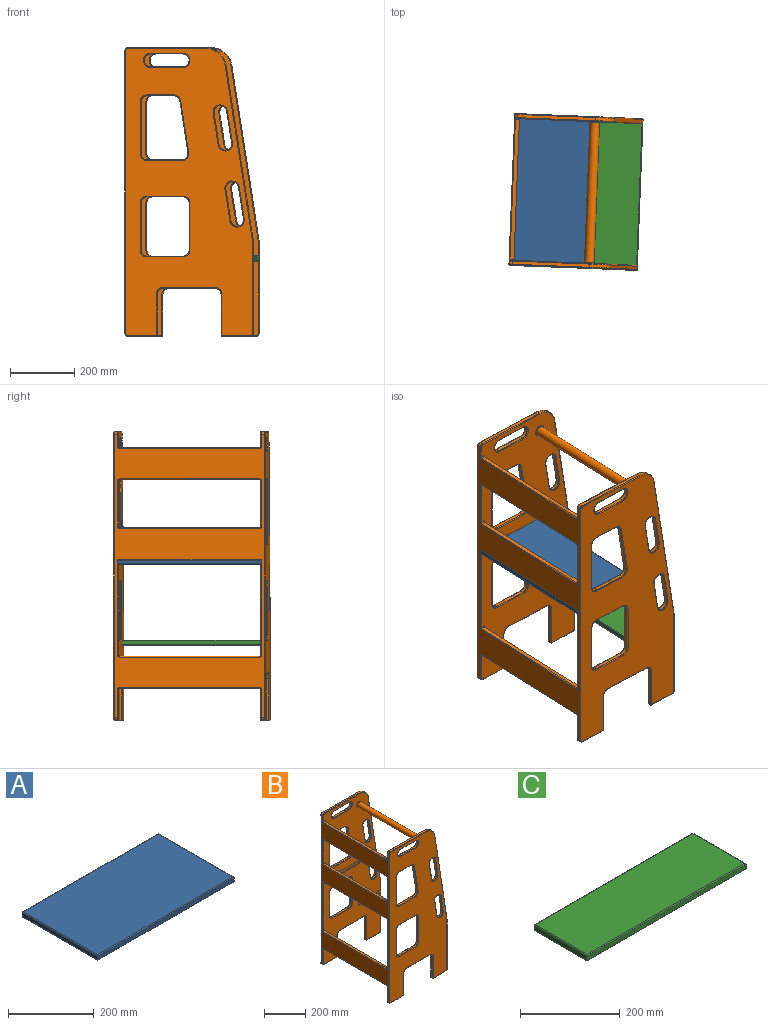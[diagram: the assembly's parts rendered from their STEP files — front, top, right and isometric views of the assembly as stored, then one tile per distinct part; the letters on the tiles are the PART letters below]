
ASSEMBLY  parts=3 mates=7
PART A: 14 faces, bbox 450x250x15 mm
  f0: plane 450x10mm, normal (0,1,0), area 4500mm2, adj f1,f3,f6,f10
  f1: plane 250x10mm, normal (-1,0,0), area 2500mm2, adj f0,f2,f7,f11
  f2: plane 450x10mm, normal (0,-1,0), area 4500mm2, adj f1,f3,f9,f13
  f3: plane 250x10mm, normal (1,0,0), area 2500mm2, adj f0,f2,f8,f12
  f4: plane 445x245mm, normal (0,0,1), area 109025mm2, adj f10,f11,f12,f13
  f5: plane 445x245mm, normal (0,0,-1), area 109025mm2, adj f6,f7,f8,f9
  f6: cylinder r=2.5mm len=450mm, axis (-1,0,0), area 1760mm2, adj f0,f5,f7,f8
  f7: cylinder r=2.5mm len=250mm, axis (0,-1,0), area 974.6mm2, adj f1,f5,f6,f9
  f8: cylinder r=2.5mm len=250mm, axis (0,1,0), area 974.6mm2, adj f3,f5,f6,f9
  f9: cylinder r=2.5mm len=450mm, axis (1,0,0), area 1760mm2, adj f2,f5,f7,f8
  f10: cylinder r=2.5mm len=450mm, axis (1,0,0), area 1760mm2, adj f0,f4,f11,f12
  f11: cylinder r=2.5mm len=250mm, axis (0,1,0), area 974.6mm2, adj f1,f4,f10,f13
  f12: cylinder r=2.5mm len=250mm, axis (0,-1,0), area 974.6mm2, adj f3,f4,f10,f13
  f13: cylinder r=2.5mm len=450mm, axis (-1,0,0), area 1760mm2, adj f2,f4,f11,f12
PART B: 341 faces, bbox 401.6x472x906.2 mm
  f0: plane 90x10mm, normal (0,0,-1), area 900mm2, adj f7,f58,f76,f109
  f1: plane 895x395mm, normal (0,-1,0), area 219137.1mm2, adj f107,f108,f109,f110,f111,f112,f113,f114
  f2: plane 895x395mm, normal (0,1,0), area 205524.9mm2, adj f62,f63,f64,f65,f66,f67,f68,f69
  f3: plane 290x10mm, normal (1,0,0), area 2892.5mm2, adj f9,f10,f22,f23,f25,f63,f71,f118
  f4: plane 240.92x10mm, normal (0,0,1), area 2409.2mm2, adj f5,f11,f77,f112
  f5: cylinder r=10mm len=10mm, axis (0,1,0), area 157.1mm2, adj f4,f6,f79,f110
  f6: plane 880x467mm, normal (-1,0,0), area 146151.2mm2, adj f5,f7,f17,f27,f28,f80,f81,f82
  f7: cylinder r=10mm len=10mm, axis (0,1,0), area 157.1mm2, adj f0,f6,f78,f107
  f8: plane 90x10mm, normal (0,0,-1), area 900mm2, adj f9,f59,f64,f121
  f9: cylinder r=10mm len=10mm, axis (0,1,0), area 157.1mm2, adj f3,f8,f62,f120
  f10: plane 545x84.86mm, normal (0.99,0,0.15), area 5515.7mm2, adj f3,f11,f73,f116
  f11: cylinder r=65mm len=64.23mm, axis (0,1,0), area 920.6mm2, adj f4,f10,f75,f114
  f12: plane 437x100mm, normal (1,0,0), area 43700mm2, adj f13,f14,f89,f255
  f13: plane 437x12.5mm, normal (0,0,1), area 5462.5mm2, adj f12,f83,f87,f253
  f14: plane 437x12.5mm, normal (0,0,-1), area 5462.5mm2, adj f12,f92,f93,f257
  f15: plane 437x97.5mm, normal (1,0,0), area 42607.5mm2, adj f16,f104,f106,f267
  f16: plane 437x12.5mm, normal (0,0,1), area 5462.5mm2, adj f15,f98,f102,f265
  f17: plane 448x250mm, normal (0,0,-1), area 5848.2mm2, adj f6,f26,f28,f103,f105,f106,f194,f196
  f18: plane 437x100mm, normal (1,0,0), area 43700mm2, adj f19,f20,f88,f254
  f19: plane 437x12.5mm, normal (0,0,1), area 5462.5mm2, adj f18,f90,f91,f256
  f20: plane 437x12.5mm, normal (0,0,-1), area 5462.5mm2, adj f18,f80,f86,f252
  f21: cylinder r=15mm len=437mm, axis (0,-1,0), area 41186.3mm2, adj f178,f340
  f22: plane 150x0.5mm, normal (0,0,-1), area 75mm2, adj f3,f24,f25,f69
  f23: plane 150x0.5mm, normal (0,0,1), area 75mm2, adj f3,f24,f25,f65
  f24: plane 15x0.5mm, normal (1,0,0), area 7.5mm2, adj f22,f23,f25,f67
  f25: plane 150x15mm, normal (0,1,0), area 2250mm2, adj f3,f22,f23,f24
  f26: plane 15x0.5mm, normal (-1,0,0), area 7.5mm2, adj f17,f27,f28,f101
  f27: plane 250x0.5mm, normal (0,0,1), area 125mm2, adj f6,f26,f28,f99
  f28: plane 250x15mm, normal (0,1,0), area 3750mm2, adj f6,f17,f26,f27
  f29: cylinder r=20mm len=39.76mm, axis (0,1,0), area 628.3mm2, adj f30,f32,f171,f175
  f30: plane 98.81x15.38mm, normal (0.99,0,0.15), area 1000mm2, adj f29,f31,f173,f177
  f31: cylinder r=20mm len=39.76mm, axis (0,1,0), area 628.3mm2, adj f30,f32,f172,f176
  f32: plane 98.81x15.38mm, normal (-0.99,0,-0.15), area 1000mm2, adj f29,f31,f170,f174
  f33: plane 110x10mm, normal (0,0,-1), area 1100mm2, adj f34,f40,f127,f135
  f34: cylinder r=20mm len=20mm, axis (0,1,0), area 314.2mm2, adj f33,f35,f129,f137
  f35: plane 145x10mm, normal (1,0,0), area 1450mm2, adj f34,f36,f128,f136
  f36: cylinder r=20mm len=20mm, axis (0,1,0), area 314.2mm2, adj f35,f37,f126,f134
  f37: plane 110x10mm, normal (0,0,1), area 1100mm2, adj f36,f38,f124,f132
  f38: cylinder r=20mm len=20mm, axis (0,1,0), area 314.2mm2, adj f37,f39,f122,f130
  f39: plane 145x10mm, normal (-1,0,0), area 1450mm2, adj f38,f40,f123,f131
  f40: cylinder r=20mm len=20mm, axis (0,1,0), area 314.2mm2, adj f33,f39,f125,f133
  f41: plane 81.73x10mm, normal (0,0,-1), area 817.3mm2, adj f42,f48,f143,f151
  f42: cylinder r=20mm len=20mm, axis (0,1,0), area 314.2mm2, adj f41,f43,f145,f153
  f43: plane 160x10mm, normal (1,0,0), area 1600mm2, adj f42,f44,f144,f152
  f44: cylinder r=20mm len=20mm, axis (0,1,0), area 314.2mm2, adj f43,f45,f142,f150
  f45: plane 106.65x10mm, normal (0,0,1), area 1066.5mm2, adj f44,f46,f140,f148
  f46: cylinder r=20mm len=23.08mm, axis (0,1,0), area 345.1mm2, adj f45,f47,f138,f146
  f47: plane 160x24.91mm, normal (-0.99,0,-0.15), area 1619.3mm2, adj f46,f48,f139,f147
  f48: cylinder r=20mm len=19.76mm, axis (0,1,0), area 283.3mm2, adj f41,f47,f141,f149
  f49: cylinder r=20mm len=40mm, axis (0,1,0), area 628.3mm2, adj f50,f52,f155,f159
  f50: plane 100x10mm, normal (0,0,1), area 1000mm2, adj f49,f51,f157,f161
  f51: cylinder r=20mm len=40mm, axis (0,1,0), area 628.3mm2, adj f50,f52,f156,f160
  f52: plane 100x10mm, normal (0,0,-1), area 1000mm2, adj f49,f51,f154,f158
  f53: cylinder r=20mm len=39.76mm, axis (0,1,0), area 628.3mm2, adj f54,f56,f162,f166
  f54: plane 98.81x15.38mm, normal (0.99,0,0.15), area 1000mm2, adj f53,f55,f163,f167
  f55: cylinder r=20mm len=39.76mm, axis (0,1,0), area 628.3mm2, adj f54,f56,f165,f169
  f56: plane 98.81x15.38mm, normal (-0.99,0,-0.15), area 1000mm2, adj f53,f55,f164,f168
  f57: cylinder r=20mm len=20mm, axis (0,1,0), area 314.2mm2, adj f58,f61,f72,f113
  f58: plane 130x10mm, normal (1,0,0), area 1300mm2, adj f0,f57,f74,f111
  f59: plane 130x10mm, normal (-1,0,0), area 1300mm2, adj f8,f60,f66,f119
  f60: cylinder r=20mm len=20mm, axis (0,1,0), area 314.2mm2, adj f59,f61,f68,f117
  f61: plane 160x10mm, normal (0,0,-1), area 1600mm2, adj f57,f60,f70,f115
  f62: torus R=7.5mm, axis (0,-1,0), area 56.1mm2, adj f2,f9,f63,f64
  f63: cylinder r=2.5mm len=225mm, axis (0,0,1), area 880mm2, adj f2,f3,f62,f65
  f64: cylinder r=2.5mm len=90mm, axis (1,0,0), area 349.9mm2, adj f2,f8,f62,f66
  f65: cylinder r=2.5mm len=152.5mm, axis (-1,0,0), area 589mm2, adj f2,f23,f63,f67
  f66: cylinder r=2.5mm len=130mm, axis (0,0,-1), area 506.9mm2, adj f2,f59,f64,f68
  f67: cylinder r=2.5mm len=20mm, axis (0,0,1), area 66mm2, adj f2,f24,f65,f69
  f68: torus R=22.5mm, axis (0,-1,0), area 129mm2, adj f2,f60,f66,f70
  f69: cylinder r=2.5mm len=152.5mm, axis (1,0,0), area 589mm2, adj f2,f22,f67,f71
  f70: cylinder r=2.5mm len=160mm, axis (1,0,0), area 628.3mm2, adj f2,f61,f68,f72
  f71: cylinder r=2.5mm len=50mm, axis (0,0,1), area 192.5mm2, adj f2,f3,f69,f73
  f72: torus R=22.5mm, axis (0,-1,0), area 129mm2, adj f2,f57,f70,f74
  f73: cylinder r=2.5mm len=545.38mm, axis (-0.15,0,0.99), area 2165.7mm2, adj f2,f10,f71,f75
  f74: cylinder r=2.5mm len=130mm, axis (0,0,1), area 506.9mm2, adj f2,f58,f72,f76
  f75: torus R=62.5mm, axis (0,-1,0), area 356.5mm2, adj f2,f11,f73,f77
  f76: cylinder r=2.5mm len=90mm, axis (1,0,0), area 349.9mm2, adj f0,f2,f74,f78
  f77: cylinder r=2.5mm len=240.92mm, axis (-1,0,0), area 946.1mm2, adj f2,f4,f75,f79
  f78: torus R=7.5mm, axis (0,-1,0), area 56.1mm2, adj f2,f7,f76,f81
  f79: torus R=7.5mm, axis (0,-1,0), area 56.1mm2, adj f2,f5,f77,f82
  f80: cylinder r=2.5mm len=437mm, axis (0,-1,0), area 1716.1mm2, adj f6,f20,f84,f250
  f81: cylinder r=2.5mm len=87.5mm, axis (0,0,-1), area 343.6mm2, adj f2,f6,f78,f84
  f82: cylinder r=2.5mm len=37.5mm, axis (0,0,-1), area 147.3mm2, adj f2,f6,f79,f85
  f83: cylinder r=2.5mm len=437mm, axis (0,1,0), area 1716.1mm2, adj f6,f13,f85,f251
  f84: torus R=5mm, axis (1,0,0), area 21mm2, adj f6,f80,f81,f86
  f85: torus R=5mm, axis (1,0,0), area 21mm2, adj f6,f82,f83,f87
  f86: cylinder r=2.5mm len=15mm, axis (1,0,0), area 52.7mm2, adj f2,f20,f84,f88
  f87: cylinder r=2.5mm len=15mm, axis (-1,0,0), area 52.7mm2, adj f2,f13,f85,f89
  f88: cylinder r=2.5mm len=105mm, axis (0,0,1), area 399.8mm2, adj f2,f18,f86,f91
  f89: cylinder r=2.5mm len=105mm, axis (0,0,1), area 399.8mm2, adj f2,f12,f87,f92
  f90: cylinder r=2.5mm len=437mm, axis (0,1,0), area 1716.1mm2, adj f6,f19,f94,f258
  f91: cylinder r=2.5mm len=15mm, axis (-1,0,0), area 52.7mm2, adj f2,f19,f88,f94
  f92: cylinder r=2.5mm len=15mm, axis (1,0,0), area 52.7mm2, adj f2,f14,f89,f95
  f93: cylinder r=2.5mm len=437mm, axis (0,-1,0), area 1716.1mm2, adj f6,f14,f95,f259
  f94: torus R=5mm, axis (1,0,0), area 21mm2, adj f6,f90,f91,f96
  f95: torus R=5mm, axis (1,0,0), area 21mm2, adj f6,f92,f93,f97
  f96: cylinder r=2.5mm len=282.5mm, axis (0,0,-1), area 1105.8mm2, adj f2,f6,f94,f99
  f97: cylinder r=2.5mm len=145mm, axis (0,0,-1), area 569.4mm2, adj f2,f6,f95,f100
  f98: cylinder r=2.5mm len=437mm, axis (0,1,0), area 1716.1mm2, adj f6,f16,f100,f263
  f99: cylinder r=2.5mm len=252.5mm, axis (-1,0,0), area 981.7mm2, adj f2,f27,f96,f101
  f100: torus R=5mm, axis (1,0,0), area 21mm2, adj f6,f97,f98,f102
  f101: cylinder r=2.5mm len=20mm, axis (0,0,-1), area 66mm2, adj f2,f26,f99,f103
  f102: cylinder r=2.5mm len=15mm, axis (-1,0,0), area 52.7mm2, adj f2,f16,f100,f104
  f103: cylinder r=2.5mm len=235mm, axis (-1,0,0), area 916.6mm2, adj f2,f17,f101,f105
  f104: cylinder r=2.5mm len=100mm, axis (0,0,1), area 386.4mm2, adj f2,f15,f102,f105
  f105: torus R=5mm, axis (0,0,1), area 21mm2, adj f17,f103,f104,f106
  f106: cylinder r=2.5mm len=437mm, axis (0,-1,0), area 1716.1mm2, adj f15,f17,f105,f268
  f107: torus R=7.5mm, axis (0,-1,0), area 56.1mm2, adj f1,f7,f108,f109
  f108: cylinder r=2.5mm len=880mm, axis (0,0,1), area 3455.8mm2, adj f1,f6,f107,f110
  f109: cylinder r=2.5mm len=90mm, axis (-1,0,0), area 349.9mm2, adj f0,f1,f107,f111
  f110: torus R=7.5mm, axis (0,-1,0), area 56.1mm2, adj f1,f5,f108,f112
  f111: cylinder r=2.5mm len=130mm, axis (0,0,-1), area 506.9mm2, adj f1,f58,f109,f113
  f112: cylinder r=2.5mm len=240.92mm, axis (1,0,0), area 946.1mm2, adj f1,f4,f110,f114
  f113: torus R=22.5mm, axis (0,-1,0), area 129mm2, adj f1,f57,f111,f115
  f114: torus R=62.5mm, axis (0,-1,0), area 356.5mm2, adj f1,f11,f112,f116
  f115: cylinder r=2.5mm len=160mm, axis (-1,0,0), area 628.3mm2, adj f1,f61,f113,f117
  f116: cylinder r=2.5mm len=545.38mm, axis (0.15,0,-0.99), area 2165.7mm2, adj f1,f10,f114,f118
  f117: torus R=22.5mm, axis (0,-1,0), area 129mm2, adj f1,f60,f115,f119
  f118: cylinder r=2.5mm len=290mm, axis (0,0,-1), area 1138.6mm2, adj f1,f3,f116,f120
  f119: cylinder r=2.5mm len=130mm, axis (0,0,1), area 506.9mm2, adj f1,f59,f117,f121
  f120: torus R=7.5mm, axis (0,-1,0), area 56.1mm2, adj f1,f9,f118,f121
  f121: cylinder r=2.5mm len=90mm, axis (-1,0,0), area 349.9mm2, adj f1,f8,f119,f120
  f122: torus R=22.5mm, axis (0,-1,0), area 129mm2, adj f2,f38,f123,f124
  f123: cylinder r=2.5mm len=145mm, axis (0,0,-1), area 569.4mm2, adj f2,f39,f122,f125
  f124: cylinder r=2.5mm len=110mm, axis (-1,0,0), area 432mm2, adj f2,f37,f122,f126
  f125: torus R=22.5mm, axis (0,-1,0), area 129mm2, adj f2,f40,f123,f127
  f126: torus R=22.5mm, axis (0,-1,0), area 129mm2, adj f2,f36,f124,f128
  f127: cylinder r=2.5mm len=110mm, axis (1,0,0), area 432mm2, adj f2,f33,f125,f129
  f128: cylinder r=2.5mm len=145mm, axis (0,0,1), area 569.4mm2, adj f2,f35,f126,f129
  f129: torus R=22.5mm, axis (0,-1,0), area 129mm2, adj f2,f34,f127,f128
  f130: torus R=22.5mm, axis (0,-1,0), area 129mm2, adj f1,f38,f131,f132
  f131: cylinder r=2.5mm len=145mm, axis (0,0,1), area 569.4mm2, adj f1,f39,f130,f133
  f132: cylinder r=2.5mm len=110mm, axis (1,0,0), area 432mm2, adj f1,f37,f130,f134
  f133: torus R=22.5mm, axis (0,-1,0), area 129mm2, adj f1,f40,f131,f135
  f134: torus R=22.5mm, axis (0,-1,0), area 129mm2, adj f1,f36,f132,f136
  f135: cylinder r=2.5mm len=110mm, axis (-1,0,0), area 432mm2, adj f1,f33,f133,f137
  f136: cylinder r=2.5mm len=145mm, axis (0,0,-1), area 569.4mm2, adj f1,f35,f134,f137
  f137: torus R=22.5mm, axis (0,-1,0), area 129mm2, adj f1,f34,f135,f136
  f138: torus R=22.5mm, axis (0,-1,0), area 141.7mm2, adj f2,f46,f139,f140
  f139: cylinder r=2.5mm len=160.38mm, axis (0.15,0,-0.99), area 635.9mm2, adj f2,f47,f138,f141
  f140: cylinder r=2.5mm len=106.65mm, axis (-1,0,0), area 418.8mm2, adj f2,f45,f138,f142
  f141: torus R=22.5mm, axis (0,-1,0), area 116.3mm2, adj f2,f48,f139,f143
  f142: torus R=22.5mm, axis (0,-1,0), area 129mm2, adj f2,f44,f140,f144
  f143: cylinder r=2.5mm len=81.73mm, axis (1,0,0), area 321mm2, adj f2,f41,f141,f145
  f144: cylinder r=2.5mm len=160mm, axis (0,0,1), area 628.3mm2, adj f2,f43,f142,f145
  f145: torus R=22.5mm, axis (0,-1,0), area 129mm2, adj f2,f42,f143,f144
  f146: torus R=22.5mm, axis (0,-1,0), area 141.7mm2, adj f1,f46,f147,f148
  f147: cylinder r=2.5mm len=160.38mm, axis (-0.15,0,0.99), area 635.9mm2, adj f1,f47,f146,f149
  f148: cylinder r=2.5mm len=106.65mm, axis (1,0,0), area 418.8mm2, adj f1,f45,f146,f150
  f149: torus R=22.5mm, axis (0,-1,0), area 116.3mm2, adj f1,f48,f147,f151
  f150: torus R=22.5mm, axis (0,-1,0), area 129mm2, adj f1,f44,f148,f152
  f151: cylinder r=2.5mm len=81.73mm, axis (-1,0,0), area 321mm2, adj f1,f41,f149,f153
  f152: cylinder r=2.5mm len=160mm, axis (0,0,-1), area 628.3mm2, adj f1,f43,f150,f153
  f153: torus R=22.5mm, axis (0,-1,0), area 129mm2, adj f1,f42,f151,f152
  f154: cylinder r=2.5mm len=100mm, axis (1,0,0), area 392.7mm2, adj f2,f52,f155,f156
  f155: torus R=22.5mm, axis (0,-1,0), area 257.9mm2, adj f2,f49,f154,f157
  f156: torus R=22.5mm, axis (0,-1,0), area 257.9mm2, adj f2,f51,f154,f157
  f157: cylinder r=2.5mm len=100mm, axis (-1,0,0), area 392.7mm2, adj f2,f50,f155,f156
  f158: cylinder r=2.5mm len=100mm, axis (-1,0,0), area 392.7mm2, adj f1,f52,f159,f160
  f159: torus R=22.5mm, axis (0,-1,0), area 257.9mm2, adj f1,f49,f158,f161
  f160: torus R=22.5mm, axis (0,-1,0), area 257.9mm2, adj f1,f51,f158,f161
  f161: cylinder r=2.5mm len=100mm, axis (1,0,0), area 392.7mm2, adj f1,f50,f159,f160
  f162: torus R=22.5mm, axis (0,-1,0), area 257.9mm2, adj f2,f53,f163,f164
  f163: cylinder r=2.5mm len=99.19mm, axis (-0.15,0,0.99), area 392.7mm2, adj f2,f54,f162,f165
  f164: cylinder r=2.5mm len=99.19mm, axis (0.15,0,-0.99), area 392.7mm2, adj f2,f56,f162,f165
  f165: torus R=22.5mm, axis (0,-1,0), area 257.9mm2, adj f2,f55,f163,f164
  f166: torus R=22.5mm, axis (0,-1,0), area 257.9mm2, adj f1,f53,f167,f168
  f167: cylinder r=2.5mm len=99.19mm, axis (0.15,0,-0.99), area 392.7mm2, adj f1,f54,f166,f169
  f168: cylinder r=2.5mm len=99.19mm, axis (-0.15,0,0.99), area 392.7mm2, adj f1,f56,f166,f169
  f169: torus R=22.5mm, axis (0,-1,0), area 257.9mm2, adj f1,f55,f167,f168
  f170: cylinder r=2.5mm len=99.19mm, axis (0.15,0,-0.99), area 392.7mm2, adj f2,f32,f171,f172
  f171: torus R=22.5mm, axis (0,-1,0), area 257.9mm2, adj f2,f29,f170,f173
  f172: torus R=22.5mm, axis (0,-1,0), area 257.9mm2, adj f2,f31,f170,f173
  f173: cylinder r=2.5mm len=99.19mm, axis (-0.15,0,0.99), area 392.7mm2, adj f2,f30,f171,f172
  f174: cylinder r=2.5mm len=99.19mm, axis (-0.15,0,0.99), area 392.7mm2, adj f1,f32,f175,f176
  f175: torus R=22.5mm, axis (0,-1,0), area 257.9mm2, adj f1,f29,f174,f177
  f176: torus R=22.5mm, axis (0,-1,0), area 257.9mm2, adj f1,f31,f174,f177
  f177: cylinder r=2.5mm len=99.19mm, axis (0.15,0,-0.99), area 392.7mm2, adj f1,f30,f175,f176
  f178: torus R=17.5mm, axis (0,-1,0), area 392.5mm2, adj f2,f21
  f179: plane 90x10mm, normal (0,0,-1), area 900mm2, adj f185,f226,f244,f271
  f180: plane 895x395mm, normal (0,1,0), area 219137.1mm2, adj f269,f270,f271,f272,f273,f274,f275,f276
  f181: plane 895x395mm, normal (0,-1,0), area 205524.9mm2, adj f230,f231,f232,f233,f234,f235,f236,f237
  f182: plane 290x10mm, normal (1,0,0), area 2892.5mm2, adj f187,f188,f190,f191,f193,f231,f239,f280
  f183: plane 240.92x10mm, normal (0,0,1), area 2409.2mm2, adj f184,f189,f245,f274
  f184: cylinder r=10mm len=10mm, axis (0,-1,0), area 157.1mm2, adj f6,f183,f247,f272
  f185: cylinder r=10mm len=10mm, axis (0,-1,0), area 157.1mm2, adj f6,f179,f246,f269
  f186: plane 90x10mm, normal (0,0,-1), area 900mm2, adj f187,f227,f232,f283
  f187: cylinder r=10mm len=10mm, axis (0,-1,0), area 157.1mm2, adj f182,f186,f230,f282
  f188: plane 545x84.86mm, normal (0.99,0,0.15), area 5515.7mm2, adj f182,f189,f241,f278
  f189: cylinder r=65mm len=64.23mm, axis (0,-1,0), area 920.6mm2, adj f183,f188,f243,f276
  f190: plane 150x0.5mm, normal (0,0,-1), area 75mm2, adj f182,f192,f193,f237
  f191: plane 150x0.5mm, normal (0,0,1), area 75mm2, adj f182,f192,f193,f233
  f192: plane 15x0.5mm, normal (1,0,0), area 7.5mm2, adj f190,f191,f193,f235
  f193: plane 150x15mm, normal (0,-1,0), area 2250mm2, adj f182,f190,f191,f192
  f194: plane 15x0.5mm, normal (-1,0,0), area 7.5mm2, adj f17,f195,f196,f264
  f195: plane 250x0.5mm, normal (0,0,1), area 125mm2, adj f6,f194,f196,f262
  f196: plane 250x15mm, normal (0,-1,0), area 3750mm2, adj f6,f17,f194,f195
  f197: cylinder r=20mm len=39.76mm, axis (0,-1,0), area 628.3mm2, adj f198,f200,f333,f337
  f198: plane 98.81x15.38mm, normal (0.99,0,0.15), area 1000mm2, adj f197,f199,f335,f339
  f199: cylinder r=20mm len=39.76mm, axis (0,-1,0), area 628.3mm2, adj f198,f200,f334,f338
  f200: plane 98.81x15.38mm, normal (-0.99,0,-0.15), area 1000mm2, adj f197,f199,f332,f336
  f201: plane 110x10mm, normal (0,0,-1), area 1100mm2, adj f202,f208,f289,f297
  f202: cylinder r=20mm len=20mm, axis (0,-1,0), area 314.2mm2, adj f201,f203,f291,f299
  f203: plane 145x10mm, normal (1,0,0), area 1450mm2, adj f202,f204,f290,f298
  f204: cylinder r=20mm len=20mm, axis (0,-1,0), area 314.2mm2, adj f203,f205,f288,f296
  f205: plane 110x10mm, normal (0,0,1), area 1100mm2, adj f204,f206,f286,f294
  f206: cylinder r=20mm len=20mm, axis (0,-1,0), area 314.2mm2, adj f205,f207,f284,f292
  f207: plane 145x10mm, normal (-1,0,0), area 1450mm2, adj f206,f208,f285,f293
  f208: cylinder r=20mm len=20mm, axis (0,-1,0), area 314.2mm2, adj f201,f207,f287,f295
  f209: plane 81.73x10mm, normal (0,0,-1), area 817.3mm2, adj f210,f216,f305,f313
  f210: cylinder r=20mm len=20mm, axis (0,-1,0), area 314.2mm2, adj f209,f211,f307,f315
  f211: plane 160x10mm, normal (1,0,0), area 1600mm2, adj f210,f212,f306,f314
  f212: cylinder r=20mm len=20mm, axis (0,-1,0), area 314.2mm2, adj f211,f213,f304,f312
  f213: plane 106.65x10mm, normal (0,0,1), area 1066.5mm2, adj f212,f214,f302,f310
  f214: cylinder r=20mm len=23.08mm, axis (0,-1,0), area 345.1mm2, adj f213,f215,f300,f308
  f215: plane 160x24.91mm, normal (-0.99,0,-0.15), area 1619.3mm2, adj f214,f216,f301,f309
  f216: cylinder r=20mm len=19.76mm, axis (0,-1,0), area 283.3mm2, adj f209,f215,f303,f311
  f217: cylinder r=20mm len=40mm, axis (0,-1,0), area 628.3mm2, adj f218,f220,f317,f321
  f218: plane 100x10mm, normal (0,0,1), area 1000mm2, adj f217,f219,f319,f323
  f219: cylinder r=20mm len=40mm, axis (0,-1,0), area 628.3mm2, adj f218,f220,f318,f322
  f220: plane 100x10mm, normal (0,0,-1), area 1000mm2, adj f217,f219,f316,f320
  f221: cylinder r=20mm len=39.76mm, axis (0,-1,0), area 628.3mm2, adj f222,f224,f324,f328
  f222: plane 98.81x15.38mm, normal (0.99,0,0.15), area 1000mm2, adj f221,f223,f325,f329
  f223: cylinder r=20mm len=39.76mm, axis (0,-1,0), area 628.3mm2, adj f222,f224,f327,f331
  f224: plane 98.81x15.38mm, normal (-0.99,0,-0.15), area 1000mm2, adj f221,f223,f326,f330
  f225: cylinder r=20mm len=20mm, axis (0,-1,0), area 314.2mm2, adj f226,f229,f240,f275
  f226: plane 130x10mm, normal (1,0,0), area 1300mm2, adj f179,f225,f242,f273
  f227: plane 130x10mm, normal (-1,0,0), area 1300mm2, adj f186,f228,f234,f281
  f228: cylinder r=20mm len=20mm, axis (0,-1,0), area 314.2mm2, adj f227,f229,f236,f279
  f229: plane 160x10mm, normal (0,0,-1), area 1600mm2, adj f225,f228,f238,f277
  f230: torus R=7.5mm, axis (0,1,0), area 56.1mm2, adj f181,f187,f231,f232
  f231: cylinder r=2.5mm len=225mm, axis (0,0,1), area 880mm2, adj f181,f182,f230,f233
  f232: cylinder r=2.5mm len=90mm, axis (1,0,0), area 349.9mm2, adj f181,f186,f230,f234
  f233: cylinder r=2.5mm len=152.5mm, axis (-1,0,0), area 589mm2, adj f181,f191,f231,f235
  f234: cylinder r=2.5mm len=130mm, axis (0,0,-1), area 506.9mm2, adj f181,f227,f232,f236
  f235: cylinder r=2.5mm len=20mm, axis (0,0,1), area 66mm2, adj f181,f192,f233,f237
  f236: torus R=22.5mm, axis (0,1,0), area 129mm2, adj f181,f228,f234,f238
  f237: cylinder r=2.5mm len=152.5mm, axis (1,0,0), area 589mm2, adj f181,f190,f235,f239
  f238: cylinder r=2.5mm len=160mm, axis (1,0,0), area 628.3mm2, adj f181,f229,f236,f240
  f239: cylinder r=2.5mm len=50mm, axis (0,0,1), area 192.5mm2, adj f181,f182,f237,f241
  f240: torus R=22.5mm, axis (0,1,0), area 129mm2, adj f181,f225,f238,f242
  f241: cylinder r=2.5mm len=545.38mm, axis (-0.15,0,0.99), area 2165.7mm2, adj f181,f188,f239,f243
  f242: cylinder r=2.5mm len=130mm, axis (0,0,1), area 506.9mm2, adj f181,f226,f240,f244
  f243: torus R=62.5mm, axis (0,1,0), area 356.5mm2, adj f181,f189,f241,f245
  f244: cylinder r=2.5mm len=90mm, axis (1,0,0), area 349.9mm2, adj f179,f181,f242,f246
  f245: cylinder r=2.5mm len=240.92mm, axis (-1,0,0), area 946.1mm2, adj f181,f183,f243,f247
  f246: torus R=7.5mm, axis (0,1,0), area 56.1mm2, adj f181,f185,f244,f248
  f247: torus R=7.5mm, axis (0,1,0), area 56.1mm2, adj f181,f184,f245,f249
  f248: cylinder r=2.5mm len=87.5mm, axis (0,0,-1), area 343.6mm2, adj f6,f181,f246,f250
  f249: cylinder r=2.5mm len=37.5mm, axis (0,0,-1), area 147.3mm2, adj f6,f181,f247,f251
  f250: torus R=5mm, axis (1,0,0), area 21mm2, adj f6,f80,f248,f252
  f251: torus R=5mm, axis (1,0,0), area 21mm2, adj f6,f83,f249,f253
  f252: cylinder r=2.5mm len=15mm, axis (1,0,0), area 52.7mm2, adj f20,f181,f250,f254
  f253: cylinder r=2.5mm len=15mm, axis (-1,0,0), area 52.7mm2, adj f13,f181,f251,f255
  f254: cylinder r=2.5mm len=105mm, axis (0,0,1), area 399.8mm2, adj f18,f181,f252,f256
  f255: cylinder r=2.5mm len=105mm, axis (0,0,1), area 399.8mm2, adj f12,f181,f253,f257
  f256: cylinder r=2.5mm len=15mm, axis (-1,0,0), area 52.7mm2, adj f19,f181,f254,f258
  f257: cylinder r=2.5mm len=15mm, axis (1,0,0), area 52.7mm2, adj f14,f181,f255,f259
  f258: torus R=5mm, axis (1,0,0), area 21mm2, adj f6,f90,f256,f260
  f259: torus R=5mm, axis (1,0,0), area 21mm2, adj f6,f93,f257,f261
  f260: cylinder r=2.5mm len=282.5mm, axis (0,0,-1), area 1105.8mm2, adj f6,f181,f258,f262
  f261: cylinder r=2.5mm len=145mm, axis (0,0,-1), area 569.4mm2, adj f6,f181,f259,f263
  f262: cylinder r=2.5mm len=252.5mm, axis (-1,0,0), area 981.7mm2, adj f181,f195,f260,f264
  f263: torus R=5mm, axis (1,0,0), area 21mm2, adj f6,f98,f261,f265
  f264: cylinder r=2.5mm len=20mm, axis (0,0,-1), area 66mm2, adj f181,f194,f262,f266
  f265: cylinder r=2.5mm len=15mm, axis (-1,0,0), area 52.7mm2, adj f16,f181,f263,f267
  f266: cylinder r=2.5mm len=235mm, axis (-1,0,0), area 916.6mm2, adj f17,f181,f264,f268
  f267: cylinder r=2.5mm len=100mm, axis (0,0,1), area 386.4mm2, adj f15,f181,f265,f268
  f268: torus R=5mm, axis (0,0,1), area 21mm2, adj f17,f106,f266,f267
  f269: torus R=7.5mm, axis (0,1,0), area 56.1mm2, adj f180,f185,f270,f271
  f270: cylinder r=2.5mm len=880mm, axis (0,0,1), area 3455.8mm2, adj f6,f180,f269,f272
  f271: cylinder r=2.5mm len=90mm, axis (-1,0,0), area 349.9mm2, adj f179,f180,f269,f273
  f272: torus R=7.5mm, axis (0,1,0), area 56.1mm2, adj f180,f184,f270,f274
  f273: cylinder r=2.5mm len=130mm, axis (0,0,-1), area 506.9mm2, adj f180,f226,f271,f275
  f274: cylinder r=2.5mm len=240.92mm, axis (1,0,0), area 946.1mm2, adj f180,f183,f272,f276
  f275: torus R=22.5mm, axis (0,1,0), area 129mm2, adj f180,f225,f273,f277
  f276: torus R=62.5mm, axis (0,1,0), area 356.5mm2, adj f180,f189,f274,f278
  f277: cylinder r=2.5mm len=160mm, axis (-1,0,0), area 628.3mm2, adj f180,f229,f275,f279
  f278: cylinder r=2.5mm len=545.38mm, axis (0.15,0,-0.99), area 2165.7mm2, adj f180,f188,f276,f280
  f279: torus R=22.5mm, axis (0,1,0), area 129mm2, adj f180,f228,f277,f281
  f280: cylinder r=2.5mm len=290mm, axis (0,0,-1), area 1138.6mm2, adj f180,f182,f278,f282
  f281: cylinder r=2.5mm len=130mm, axis (0,0,1), area 506.9mm2, adj f180,f227,f279,f283
  f282: torus R=7.5mm, axis (0,1,0), area 56.1mm2, adj f180,f187,f280,f283
  f283: cylinder r=2.5mm len=90mm, axis (-1,0,0), area 349.9mm2, adj f180,f186,f281,f282
  f284: torus R=22.5mm, axis (0,1,0), area 129mm2, adj f181,f206,f285,f286
  f285: cylinder r=2.5mm len=145mm, axis (0,0,-1), area 569.4mm2, adj f181,f207,f284,f287
  f286: cylinder r=2.5mm len=110mm, axis (-1,0,0), area 432mm2, adj f181,f205,f284,f288
  f287: torus R=22.5mm, axis (0,1,0), area 129mm2, adj f181,f208,f285,f289
  f288: torus R=22.5mm, axis (0,1,0), area 129mm2, adj f181,f204,f286,f290
  f289: cylinder r=2.5mm len=110mm, axis (1,0,0), area 432mm2, adj f181,f201,f287,f291
  f290: cylinder r=2.5mm len=145mm, axis (0,0,1), area 569.4mm2, adj f181,f203,f288,f291
  f291: torus R=22.5mm, axis (0,1,0), area 129mm2, adj f181,f202,f289,f290
  f292: torus R=22.5mm, axis (0,1,0), area 129mm2, adj f180,f206,f293,f294
  f293: cylinder r=2.5mm len=145mm, axis (0,0,1), area 569.4mm2, adj f180,f207,f292,f295
  f294: cylinder r=2.5mm len=110mm, axis (1,0,0), area 432mm2, adj f180,f205,f292,f296
  f295: torus R=22.5mm, axis (0,1,0), area 129mm2, adj f180,f208,f293,f297
  f296: torus R=22.5mm, axis (0,1,0), area 129mm2, adj f180,f204,f294,f298
  f297: cylinder r=2.5mm len=110mm, axis (-1,0,0), area 432mm2, adj f180,f201,f295,f299
  f298: cylinder r=2.5mm len=145mm, axis (0,0,-1), area 569.4mm2, adj f180,f203,f296,f299
  f299: torus R=22.5mm, axis (0,1,0), area 129mm2, adj f180,f202,f297,f298
  f300: torus R=22.5mm, axis (0,1,0), area 141.7mm2, adj f181,f214,f301,f302
  f301: cylinder r=2.5mm len=160.38mm, axis (0.15,0,-0.99), area 635.9mm2, adj f181,f215,f300,f303
  f302: cylinder r=2.5mm len=106.65mm, axis (-1,0,0), area 418.8mm2, adj f181,f213,f300,f304
  f303: torus R=22.5mm, axis (0,1,0), area 116.3mm2, adj f181,f216,f301,f305
  f304: torus R=22.5mm, axis (0,1,0), area 129mm2, adj f181,f212,f302,f306
  f305: cylinder r=2.5mm len=81.73mm, axis (1,0,0), area 321mm2, adj f181,f209,f303,f307
  f306: cylinder r=2.5mm len=160mm, axis (0,0,1), area 628.3mm2, adj f181,f211,f304,f307
  f307: torus R=22.5mm, axis (0,1,0), area 129mm2, adj f181,f210,f305,f306
  f308: torus R=22.5mm, axis (0,1,0), area 141.7mm2, adj f180,f214,f309,f310
  f309: cylinder r=2.5mm len=160.38mm, axis (-0.15,0,0.99), area 635.9mm2, adj f180,f215,f308,f311
  f310: cylinder r=2.5mm len=106.65mm, axis (1,0,0), area 418.8mm2, adj f180,f213,f308,f312
  f311: torus R=22.5mm, axis (0,1,0), area 116.3mm2, adj f180,f216,f309,f313
  f312: torus R=22.5mm, axis (0,1,0), area 129mm2, adj f180,f212,f310,f314
  f313: cylinder r=2.5mm len=81.73mm, axis (-1,0,0), area 321mm2, adj f180,f209,f311,f315
  f314: cylinder r=2.5mm len=160mm, axis (0,0,-1), area 628.3mm2, adj f180,f211,f312,f315
  f315: torus R=22.5mm, axis (0,1,0), area 129mm2, adj f180,f210,f313,f314
  f316: cylinder r=2.5mm len=100mm, axis (1,0,0), area 392.7mm2, adj f181,f220,f317,f318
  f317: torus R=22.5mm, axis (0,1,0), area 257.9mm2, adj f181,f217,f316,f319
  f318: torus R=22.5mm, axis (0,1,0), area 257.9mm2, adj f181,f219,f316,f319
  f319: cylinder r=2.5mm len=100mm, axis (-1,0,0), area 392.7mm2, adj f181,f218,f317,f318
  f320: cylinder r=2.5mm len=100mm, axis (-1,0,0), area 392.7mm2, adj f180,f220,f321,f322
  f321: torus R=22.5mm, axis (0,1,0), area 257.9mm2, adj f180,f217,f320,f323
  f322: torus R=22.5mm, axis (0,1,0), area 257.9mm2, adj f180,f219,f320,f323
  f323: cylinder r=2.5mm len=100mm, axis (1,0,0), area 392.7mm2, adj f180,f218,f321,f322
  f324: torus R=22.5mm, axis (0,1,0), area 257.9mm2, adj f181,f221,f325,f326
  f325: cylinder r=2.5mm len=99.19mm, axis (-0.15,0,0.99), area 392.7mm2, adj f181,f222,f324,f327
  f326: cylinder r=2.5mm len=99.19mm, axis (0.15,0,-0.99), area 392.7mm2, adj f181,f224,f324,f327
  f327: torus R=22.5mm, axis (0,1,0), area 257.9mm2, adj f181,f223,f325,f326
  f328: torus R=22.5mm, axis (0,1,0), area 257.9mm2, adj f180,f221,f329,f330
  f329: cylinder r=2.5mm len=99.19mm, axis (0.15,0,-0.99), area 392.7mm2, adj f180,f222,f328,f331
  f330: cylinder r=2.5mm len=99.19mm, axis (-0.15,0,0.99), area 392.7mm2, adj f180,f224,f328,f331
  f331: torus R=22.5mm, axis (0,1,0), area 257.9mm2, adj f180,f223,f329,f330
  f332: cylinder r=2.5mm len=99.19mm, axis (0.15,0,-0.99), area 392.7mm2, adj f181,f200,f333,f334
  f333: torus R=22.5mm, axis (0,1,0), area 257.9mm2, adj f181,f197,f332,f335
  f334: torus R=22.5mm, axis (0,1,0), area 257.9mm2, adj f181,f199,f332,f335
  f335: cylinder r=2.5mm len=99.19mm, axis (-0.15,0,0.99), area 392.7mm2, adj f181,f198,f333,f334
  f336: cylinder r=2.5mm len=99.19mm, axis (-0.15,0,0.99), area 392.7mm2, adj f180,f200,f337,f338
  f337: torus R=22.5mm, axis (0,1,0), area 257.9mm2, adj f180,f197,f336,f339
  f338: torus R=22.5mm, axis (0,1,0), area 257.9mm2, adj f180,f199,f336,f339
  f339: cylinder r=2.5mm len=99.19mm, axis (0.15,0,-0.99), area 392.7mm2, adj f180,f198,f337,f338
  f340: torus R=17.5mm, axis (0,1,0), area 392.5mm2, adj f21,f181
PART C: 14 faces, bbox 450x150x15 mm
  f0: plane 450x10mm, normal (0,1,0), area 4500mm2, adj f1,f3,f6,f10
  f1: plane 150x10mm, normal (-1,0,0), area 1500mm2, adj f0,f2,f7,f11
  f2: plane 450x10mm, normal (0,-1,0), area 4500mm2, adj f1,f3,f9,f13
  f3: plane 150x10mm, normal (1,0,0), area 1500mm2, adj f0,f2,f8,f12
  f4: plane 445x145mm, normal (0,0,1), area 64525mm2, adj f10,f11,f12,f13
  f5: plane 445x145mm, normal (0,0,-1), area 64525mm2, adj f6,f7,f8,f9
  f6: cylinder r=2.5mm len=450mm, axis (-1,0,0), area 1760mm2, adj f0,f5,f7,f8
  f7: cylinder r=2.5mm len=150mm, axis (0,-1,0), area 581.9mm2, adj f1,f5,f6,f9
  f8: cylinder r=2.5mm len=150mm, axis (0,1,0), area 581.9mm2, adj f3,f5,f6,f9
  f9: cylinder r=2.5mm len=450mm, axis (1,0,0), area 1760mm2, adj f2,f5,f7,f8
  f10: cylinder r=2.5mm len=450mm, axis (1,0,0), area 1760mm2, adj f0,f4,f11,f12
  f11: cylinder r=2.5mm len=150mm, axis (0,1,0), area 581.9mm2, adj f1,f4,f10,f13
  f12: cylinder r=2.5mm len=150mm, axis (0,-1,0), area 581.9mm2, adj f3,f4,f10,f13
  f13: cylinder r=2.5mm len=450mm, axis (-1,0,0), area 1760mm2, adj f2,f4,f11,f12
PLACE A rot(axis=(0,0,-1),92.2deg) t=(-395.84,77.42,619.71)mm
PLACE B rot(axis=(0,0,-1),2.2deg) t=(-254.56,-148.27,134.71)mm
PLACE C rot(axis=(0,0,-1),92.2deg) t=(-245.96,71.56,369.71)mm
MATE planar C.f5 <-> B.f191  axis (0,0,-1) through (-320.9,74.49,369.71)mm
MATE parallel C.f4 <-> A.f5  axis (0,0,1) through (-320.9,74.49,384.71)mm
MATE planar A.f1 <-> B.f196  axis (0.04,1,0) through (-511.95,307.14,627.21)mm
MATE planar A.f2 <-> B.f6  axis (-1,0.04,0) through (-645.65,87.2,627.21)mm
MATE planar C.f0 <-> B.f182  axis (1,-0.04,0) through (-245.96,71.56,377.21)mm
MATE planar B.f17 <-> A.f4  axis (0,0,-1) through (-634.28,87.75,634.71)mm
MATE planar C.f1 <-> B.f193  axis (0.04,1,0) through (-312.1,299.32,377.21)mm
